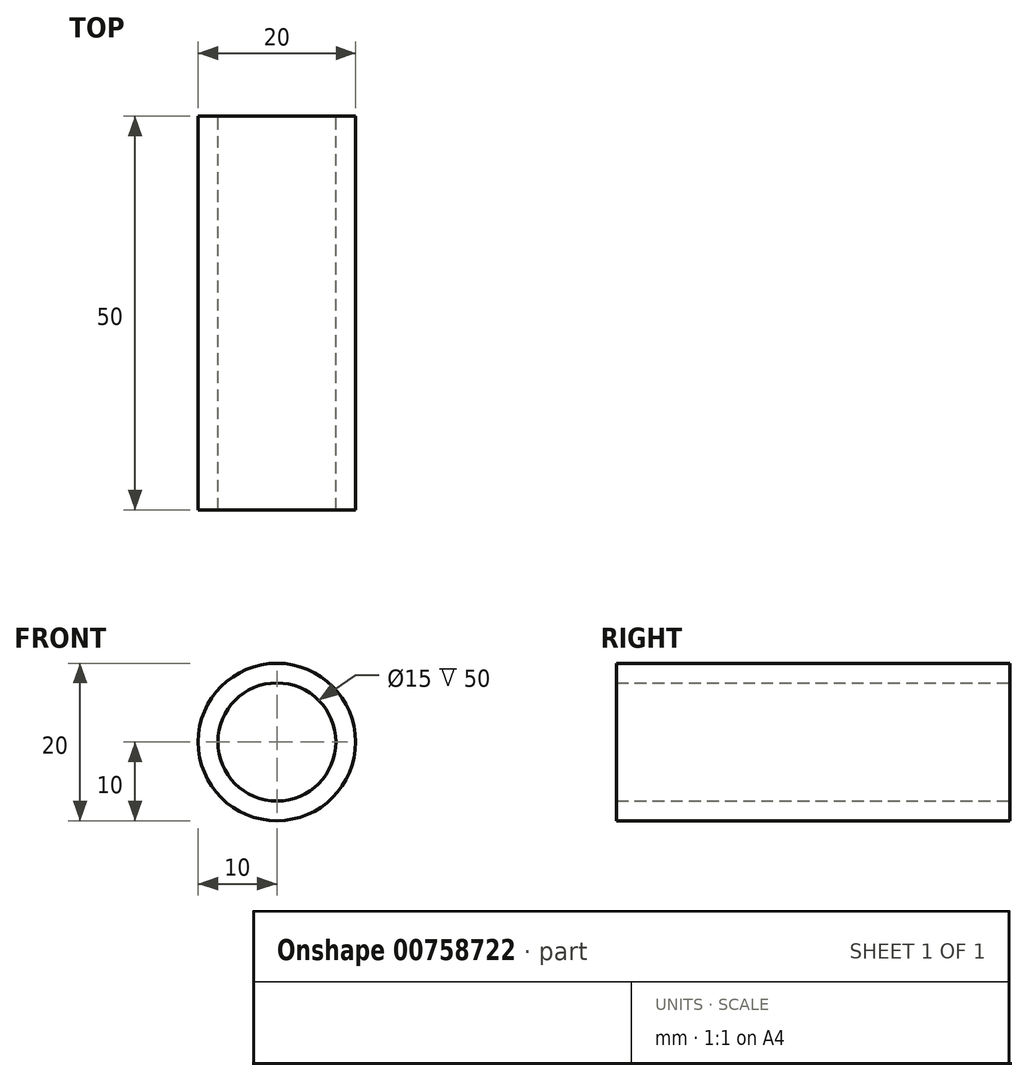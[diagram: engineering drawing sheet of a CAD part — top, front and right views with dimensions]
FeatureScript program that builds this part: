
annotation { "Feature Type Name" : "Feature", "Feature Type Description" : "" }
export const myFeature = defineFeature(function(context is Context, id is Id, definition is map)
    precondition{}
    {
        {
            var Q0;
            Q0=qCreatedBy(makeId("Front.planeOp"),FACE);
            var sketch = newSketch(context, id + "F0", { "sketchPlane" : qUnion([Q0])});
            skCircle(sketch, "E0", {"center": v(0, 0) * mm, "radius": 7.5 * mm});
            skCircle(sketch, "E1", {"center": v(0, 0) * mm, "radius": 10 * mm});
            skSolve(sketch);
        }
        {
            var Q0;
            Q0=makeQuery(id+"F0.imprint","IMPRINT",FACE,{"disambiguationData":[TD([[makeQuery(id+"F0.imprint","IMPRINT",EDGE,{"derivedFrom":sQuery(id+"F0.wireOp",EDGE,"E0")}),-1.0]])]});
            extrude(context, id + "F1", {"entities" : qUnion([Q0]), "depth" : 50 * mm, "offsetDistance" : 25 * mm});
        }
    });
